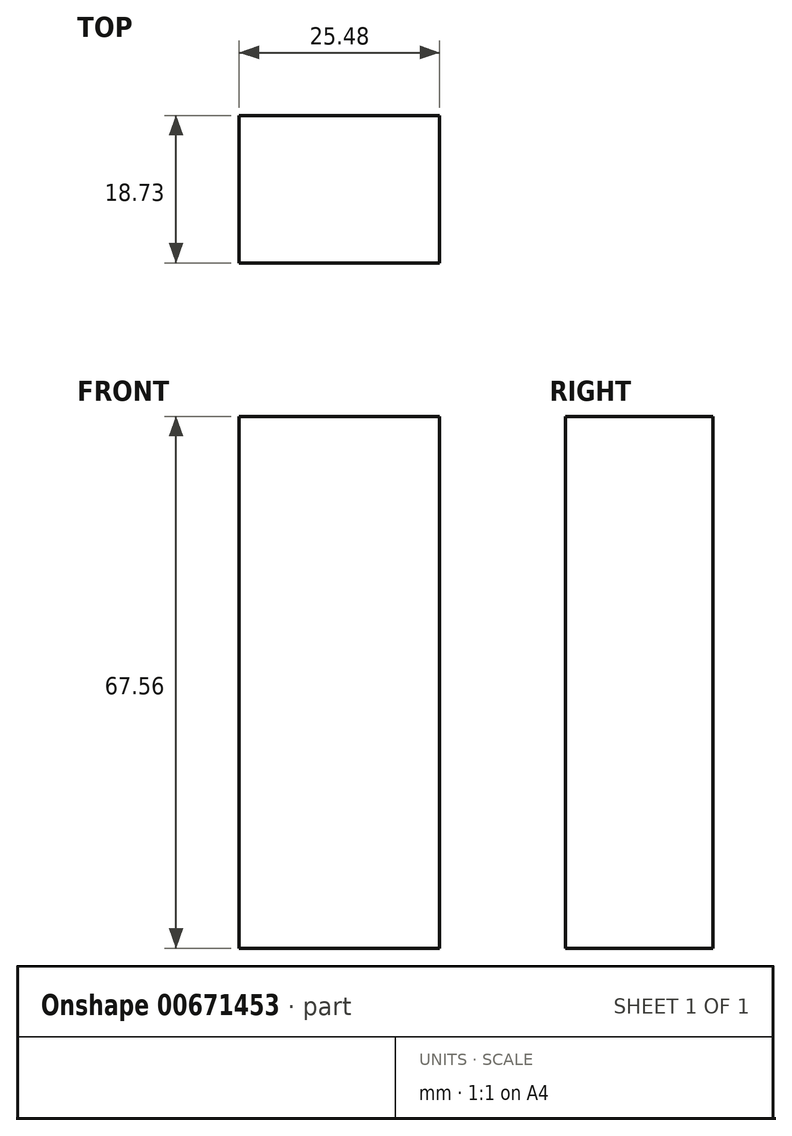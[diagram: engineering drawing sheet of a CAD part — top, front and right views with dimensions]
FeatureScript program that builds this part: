
annotation { "Feature Type Name" : "Feature", "Feature Type Description" : "" }
export const myFeature = defineFeature(function(context is Context, id is Id, definition is map)
    precondition{}
    {
        {
            var Q0;
            Q0=qCreatedBy(makeId("Front.planeOp"),FACE);
            var sketch = newSketch(context, id + "F0", { "sketchPlane" : qUnion([Q0])});
            skLineSegment(sketch, "E0.bottom", {"start": v(12.74, -33.78) * mm, "end": v(-12.74, -33.78) * mm});
            skLineSegment(sketch, "E0.top", {"start": v(12.74, 33.78) * mm, "end": v(-12.74, 33.78) * mm});
            skLineSegment(sketch, "E0.left", {"start": v(12.74, -33.78) * mm, "end": v(12.74, 33.78) * mm});
            skLineSegment(sketch, "E0.right", {"start": v(-12.74, -33.78) * mm, "end": v(-12.74, 33.78) * mm});
            skPoint(sketch, "E0.middle", {"position": v(0, 0) * mm});
            skSolve(sketch);
        }
        {
            var Q0;
            Q0=makeQuery(id+"F0.imprint","IMPRINT",FACE,{"disambiguationData":[TD([[makeQuery(id+"F0.imprint","IMPRINT",EDGE,{"derivedFrom":sQuery(id+"F0.wireOp",EDGE,"E0.bottom")}),-1.0]])]});
            extrude(context, id + "F1", {"entities" : qUnion([Q0]), "depth" : 18.73 * mm, "offsetDistance" : 25.4 * mm});
        }
    });
